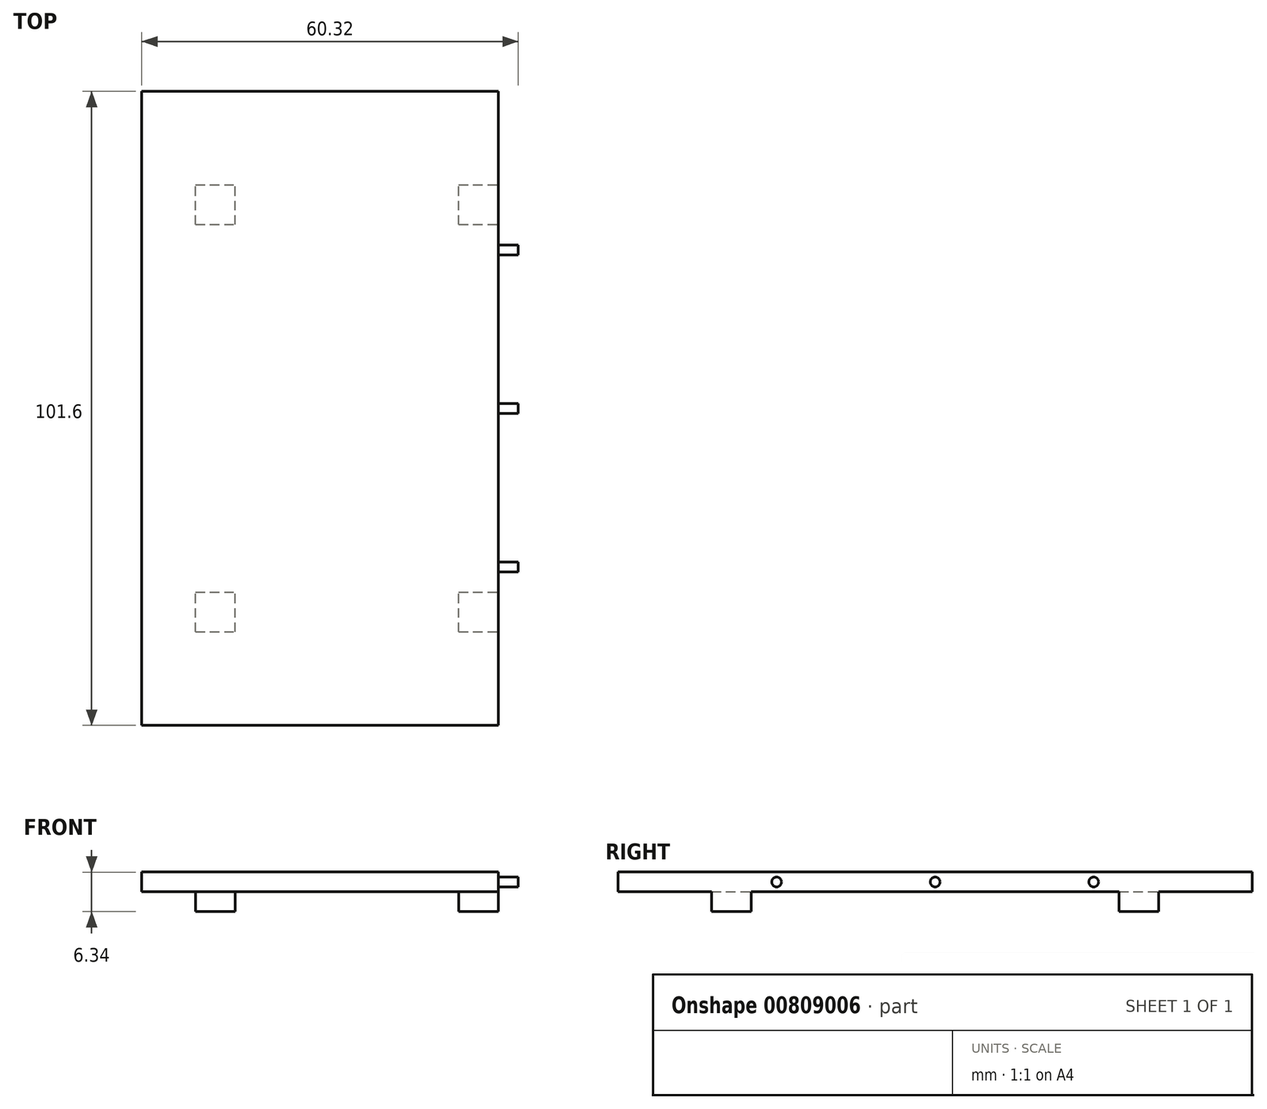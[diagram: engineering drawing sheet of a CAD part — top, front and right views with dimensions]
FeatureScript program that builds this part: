
annotation { "Feature Type Name" : "Feature", "Feature Type Description" : "" }
export const myFeature = defineFeature(function(context is Context, id is Id, definition is map)
    precondition{}
    {
        {
            var Q0;
            Q0=qCreatedBy(makeId("Top.planeOp"),FACE);
            var sketch = newSketch(context, id + "F0", { "sketchPlane" : qUnion([Q0])});
            skLineSegment(sketch, "E0.bottom", {"start": v(-28.57, 50.8) * mm, "end": v(28.58, 50.8) * mm});
            skLineSegment(sketch, "E0.top", {"start": v(-28.58, -50.8) * mm, "end": v(28.57, -50.8) * mm});
            skLineSegment(sketch, "E0.left", {"start": v(-28.57, 50.8) * mm, "end": v(-28.58, -50.8) * mm});
            skLineSegment(sketch, "E0.right", {"start": v(28.58, 50.8) * mm, "end": v(28.57, -50.8) * mm});
            skLineSegment(sketch, "E1", {"start": v(-28.57, 50.8) * mm, "end": v(28.57, -50.8) * mm, "construction": true});
            skLineSegment(sketch, "E2", {"start": v(-28.58, -50.8) * mm, "end": v(28.58, 50.8) * mm, "construction": true});
            skSolve(sketch);
        }
        {
            var Q0;
            Q0 = qSketchRegion(id + "F0", true);
            extrude(context, id + "F1", {"entities" : qUnion([Q0]), "depth" : 3.17 * mm, "offsetDistance" : 25.4 * mm});
        }
        {
            var Q0;
            Q0=makeQuery(id+"F1.opExtrude","SWEPT_FACE",FACE,{"disambiguationData":[OSD([sQuery(id+"F0.wireOp",EDGE,"E0.right")])]});
            var sketch = newSketch(context, id + "F2", { "sketchPlane" : qUnion([Q0])});
            skCircle(sketch, "E3", {"center": v(0, 1.59) * mm, "radius": 0.79 * mm});
            skPoint(sketch, "E3.centerSnap0", {"position": v(0, 0) * mm});
            skCircle(sketch, "E4", {"center": v(25.4, 1.59) * mm, "radius": 0.79 * mm});
            skPoint(sketch, "E4.centerSnap0", {"position": v(50.8, 1.59) * mm});
            skCircle(sketch, "E5", {"center": v(-25.4, 1.59) * mm, "radius": 0.79 * mm});
            skLineSegment(sketch, "E6", {"start": v(0, 0) * mm, "end": v(0, 3.18) * mm, "construction": true});
            skLineSegment(sketch, "E7", {"start": v(-25.4, 1.59) * mm, "end": v(0, 1.59) * mm, "construction": true});
            skLineSegment(sketch, "E8", {"start": v(25.4, 1.59) * mm, "end": v(0, 1.59) * mm, "construction": true});
            skSolve(sketch);
        }
        {
            var Q0;
            Q0 = qSketchRegion(id + "F2", true);
            extrude(context, id + "F3", {"entities" : qUnion([Q0]), "operationType" : NewBodyOperationType.ADD, "depth" : 3.17 * mm, "offsetDistance" : 25.4 * mm});
        }
        {
            var Q0;
            Q0=makeQuery(id+"F1.opExtrude","CAP_FACE",FACE,{"disambiguationData":[OSD([sQuery(id+"F0.wireOp",EDGE,"E0.bottom"),sQuery(id+"F0.wireOp",EDGE,"E0.top"),sQuery(id+"F0.wireOp",EDGE,"E0.left"),sQuery(id+"F0.wireOp",EDGE,"E0.right")])],"isStart":true});
            var sketch = newSketch(context, id + "F4", { "sketchPlane" : qUnion([Q0])});
            skLineSegment(sketch, "E9.bottom", {"start": v(-19.94, 35.81) * mm, "end": v(-13.59, 35.81) * mm});
            skLineSegment(sketch, "E9.top", {"start": v(-19.94, 29.46) * mm, "end": v(-13.59, 29.46) * mm});
            skLineSegment(sketch, "E9.left", {"start": v(-19.94, 35.81) * mm, "end": v(-19.94, 29.46) * mm});
            skLineSegment(sketch, "E9.right", {"start": v(-13.59, 35.81) * mm, "end": v(-13.59, 29.46) * mm});
            skLineSegment(sketch, "E10.bottom", {"start": v(-19.94, -29.46) * mm, "end": v(-13.59, -29.46) * mm});
            skLineSegment(sketch, "E10.top", {"start": v(-19.94, -35.81) * mm, "end": v(-13.59, -35.81) * mm});
            skLineSegment(sketch, "E10.left", {"start": v(-19.94, -29.46) * mm, "end": v(-19.94, -35.81) * mm});
            skLineSegment(sketch, "E10.right", {"start": v(-13.59, -29.46) * mm, "end": v(-13.59, -35.81) * mm});
            skLineSegment(sketch, "E11.bottom", {"start": v(22.22, -29.46) * mm, "end": v(28.58, -29.46) * mm});
            skLineSegment(sketch, "E11.top", {"start": v(22.22, -35.81) * mm, "end": v(28.57, -35.81) * mm});
            skLineSegment(sketch, "E11.left", {"start": v(22.22, -29.46) * mm, "end": v(22.22, -35.81) * mm});
            skLineSegment(sketch, "E11.right", {"start": v(28.58, -29.46) * mm, "end": v(28.58, -35.81) * mm});
            skLineSegment(sketch, "E12.bottom", {"start": v(22.22, 35.81) * mm, "end": v(28.57, 35.81) * mm});
            skLineSegment(sketch, "E12.top", {"start": v(22.22, 29.46) * mm, "end": v(28.57, 29.46) * mm});
            skLineSegment(sketch, "E12.left", {"start": v(22.22, 35.81) * mm, "end": v(22.22, 29.46) * mm});
            skLineSegment(sketch, "E12.right", {"start": v(28.57, 35.81) * mm, "end": v(28.57, 29.46) * mm});
            skSolve(sketch);
        }
        {
            var Q0;
            Q0 = qSketchRegion(id + "F4", true);
            extrude(context, id + "F5", {"entities" : qUnion([Q0]), "operationType" : NewBodyOperationType.ADD, "depth" : 3.17 * mm, "offsetDistance" : 25.4 * mm});
        }
    });
